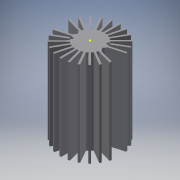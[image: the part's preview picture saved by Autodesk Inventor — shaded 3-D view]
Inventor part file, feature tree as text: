
AUTODESK INVENTOR PART (.ipt)
format: ipt  version: 2018 (Build 220112000, 112)  size: 309,248 bytes
history: native  units: mm
features: sketch x7, extrude x5, thread x3, reference x2, other x2
ambient origin geometry x8: Origin, YZ Plane, XZ Plane, XY Plane, X Axis, Y Axis, Z Axis, Center Point
bodies: Solid1 (feature_tree)
feature tree (19):
  extrude  "Extrusion1"  Depth=40.0mm TaperAngle=0.0deg
  extrude  "Extrusion2"  Depth=60.0mm TaperAngle=0.0deg
  extrude  "Extrusion3"  Depth=11.44mm
  sketch  "Sketch5"  dims[d9=11.44mm d10=0.65mm]
  sketch  "Sketch9"  dims[d11=0.65mm d12=60.0mm d13=0.0mm d14=110.0mm d16=25.900686mm d18=0.65mm d19=0.65mm]
  extrude  "Extrusion6"  Depth=0.65mm
  extrude  "Extrusion7"  Depth=60.0mm TaperAngle=0.0deg
  thread  "Thread1"  [1 undecoded]
  thread  "Thread2"  [1 undecoded]
  thread  "Thread3"  [1 undecoded]
  sketch  "Sketch1"  dims[d0=19.91mm d1=40.0mm d2=0.0mm]
  sketch  "Sketch2"  dims[d3=2.43mm d4=2.43mm d5=60.0mm d6=0.0mm]
  sketch  "Sketch3"  dims[d7=42.0116mm d8=11.44mm]
  sketch  "Sketch10"  dims[d20=110.0mm d22=25.900686mm]
  reference  "Reference4"
  reference  "Reference5"
  sketch  "Sketch11"  dims[d38=6.0mm d39=0.0mm d40=6.0mm d41=10.0mm d42=0.0mm d43=10.0mm d44=0.0mm d45=20.0mm d46=0.0mm d47=10.0mm d48=0.0mm d49=10.0mm d50=0.0mm]
  other  "Assembly1"
  other  "M850D2:1"
note: 3 required parameter values undecoded (feature->parameter linkage not recoverable at this tier; creation-order binding heuristic only, values carry confidence <= 0.55)
